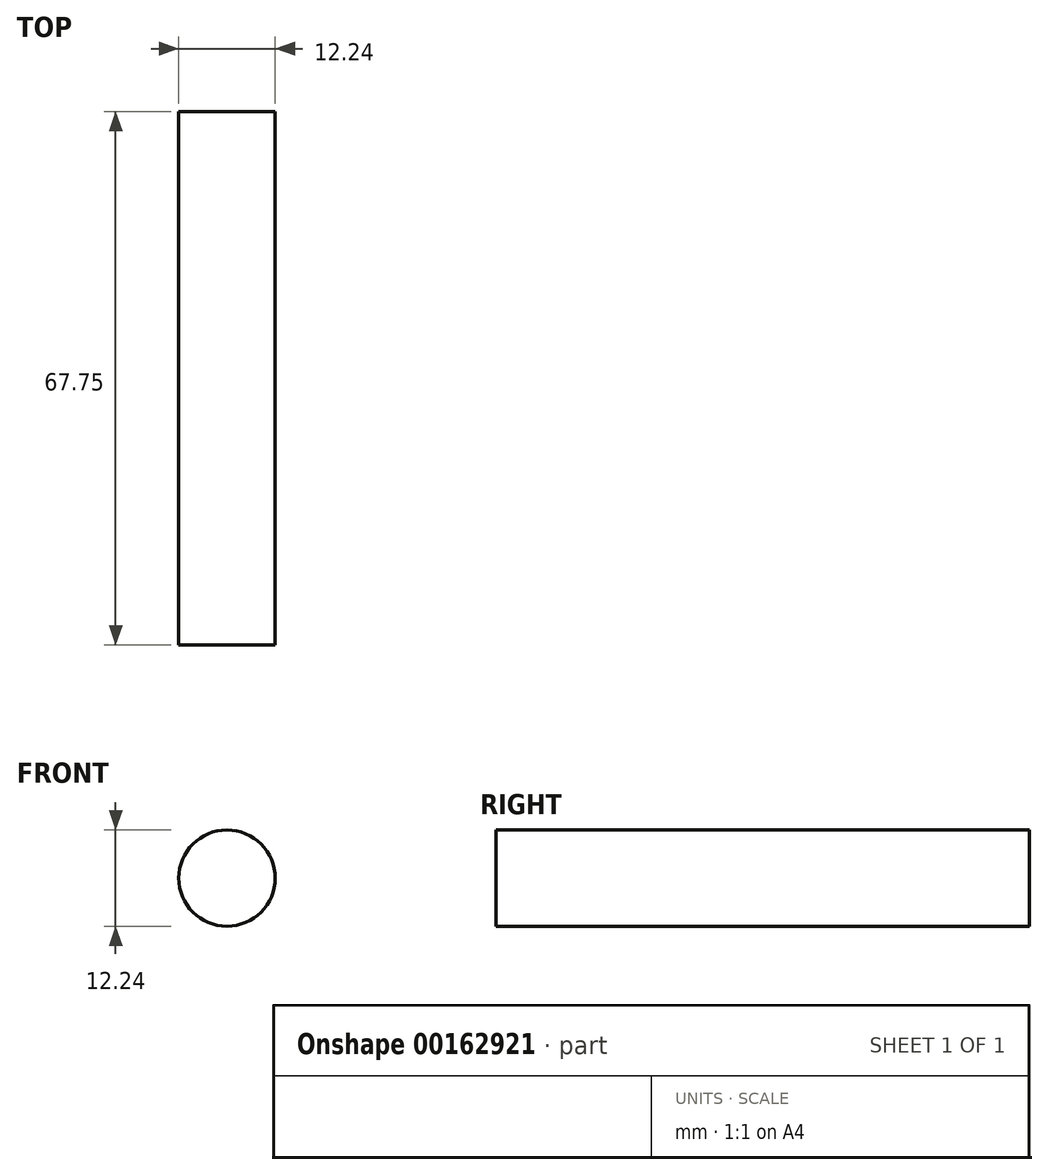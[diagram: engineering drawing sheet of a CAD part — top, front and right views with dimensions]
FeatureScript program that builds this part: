
annotation { "Feature Type Name" : "Feature", "Feature Type Description" : "" }
export const myFeature = defineFeature(function(context is Context, id is Id, definition is map)
    precondition{}
    {
        {
            var Q0;
            Q0=qCreatedBy(makeId("Front.planeOp"),FACE);
            var sketch = newSketch(context, id + "F0", { "sketchPlane" : qUnion([Q0])});
            skCircle(sketch, "E0", {"center": v(0, 0) * mm, "radius": 6.12 * mm});
            skSolve(sketch);
        }
        {
            var Q0;
            Q0=qSketchRegion(id+"F0",true);
            extrude(context, id + "F1", {"entities" : qUnion([Q0]), "depth" : 67.75 * mm});
        }
    });
